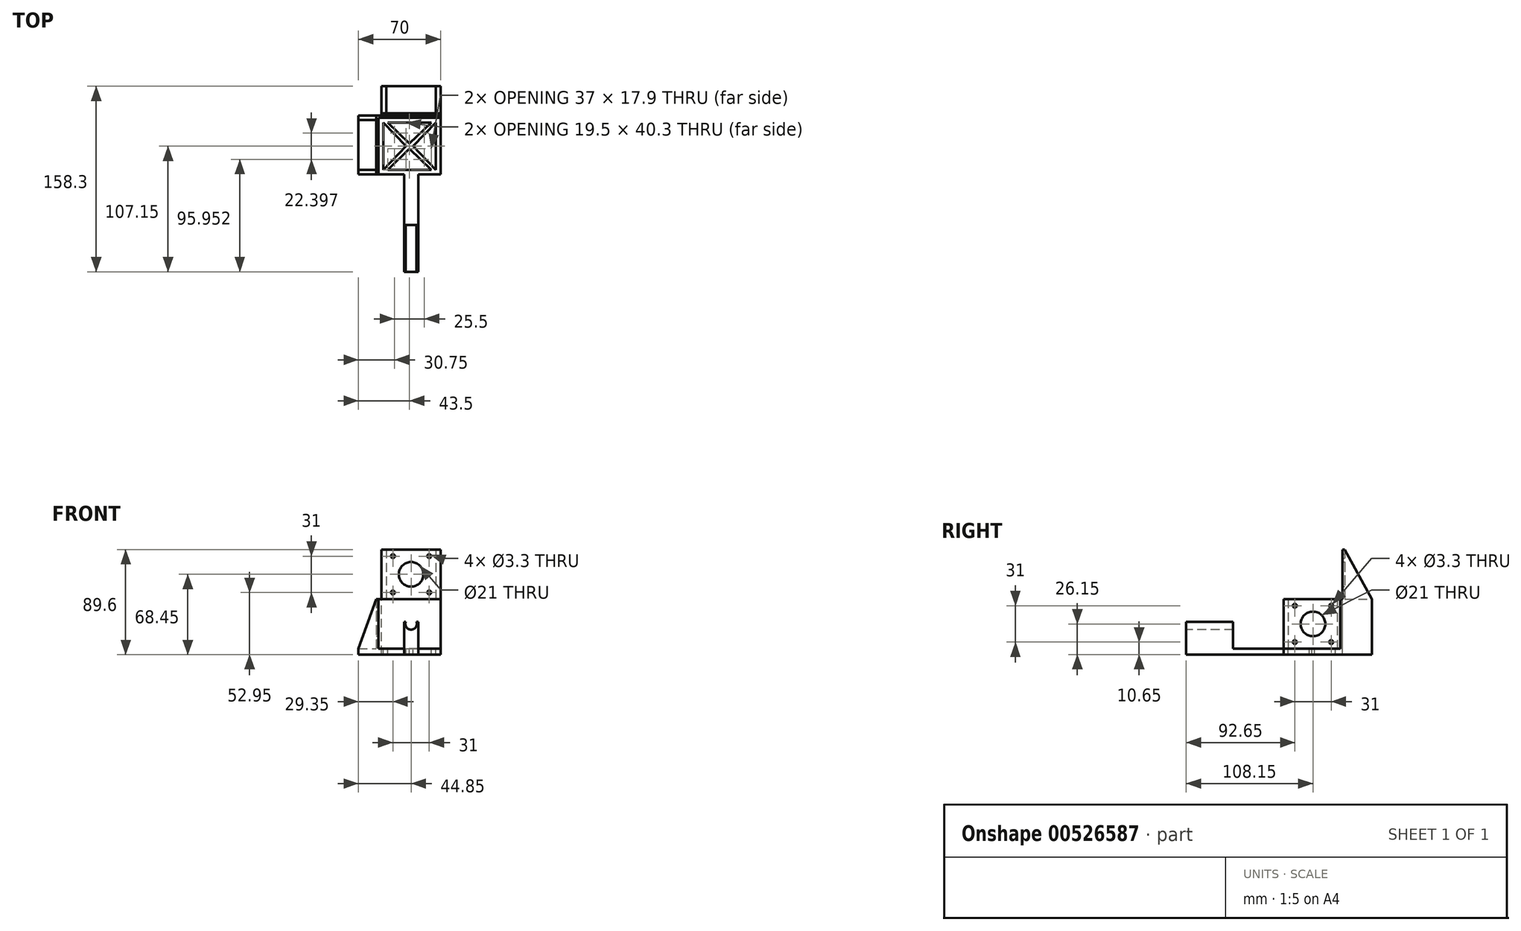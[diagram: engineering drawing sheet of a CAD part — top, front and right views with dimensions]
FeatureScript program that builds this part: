
annotation { "Feature Type Name" : "Feature", "Feature Type Description" : "" }
export const myFeature = defineFeature(function(context is Context, id is Id, definition is map)
    precondition{}
    {
        {
            var Q0;
            Q0=qCreatedBy(makeId("Top.planeOp"),FACE);
            var sketch = newSketch(context, id + "F0", { "sketchPlane" : qUnion([Q0])});
            skLineSegment(sketch, "E0.bottom", {"start": v(0, 0) * mm, "end": v(70, 0) * mm});
            skLineSegment(sketch, "E0.top", {"start": v(0, 80) * mm, "end": v(70, 80) * mm});
            skLineSegment(sketch, "E0.left", {"start": v(0, 0) * mm, "end": v(0, 80) * mm});
            skLineSegment(sketch, "E0.right", {"start": v(70, 0) * mm, "end": v(70, 80) * mm});
            skSolve(sketch);
        }
        {
            var Q0;
            Q0 = qSketchRegion(id + "F0", true);
            extrude(context, id + "F1", {"entities" : qUnion([Q0]), "depth" : 5 * mm, "offsetDistance" : 25 * mm});
        }
        {
            var Q0;
            Q0=makeQuery(id+"F1.opExtrude","CAP_FACE",FACE,{"disambiguationData":[OSD([sQuery(id+"F0.wireOp",EDGE,"E0.bottom"),sQuery(id+"F0.wireOp",EDGE,"E0.top"),sQuery(id+"F0.wireOp",EDGE,"E0.left"),sQuery(id+"F0.wireOp",EDGE,"E0.right")])],"isStart":false});
            var sketch = newSketch(context, id + "F2", { "sketchPlane" : qUnion([Q0])});
            skLineSegment(sketch, "E1.bottom", {"start": v(15, 46.3) * mm, "end": v(17, 46.3) * mm});
            skLineSegment(sketch, "E1.top", {"start": v(15, 4) * mm, "end": v(17, 4) * mm});
            skLineSegment(sketch, "E1.left", {"start": v(15, 46.3) * mm, "end": v(15, 4) * mm});
            skLineSegment(sketch, "E1.right", {"start": v(17, 46.3) * mm, "end": v(17, 4) * mm});
            skSolve(sketch);
        }
        {
            var Q0;
            Q0 = qSketchRegion(id + "F2", true);
            extrude(context, id + "F3", {"entities" : qUnion([Q0]), "operationType" : NewBodyOperationType.ADD, "depth" : 42.3 * mm, "offsetDistance" : 25 * mm});
        }
        {
            var Q0;
            Q0=makeQuery(id+"F3.opExtrude","SWEPT_FACE",FACE,{"disambiguationData":[OSD([sQuery(id+"F2.wireOp",EDGE,"E1.left")])]});
            var sketch = newSketch(context, id + "F4", { "sketchPlane" : qUnion([Q0])});
            skLineSegment(sketch, "E2.bottom", {"start": v(-9.65, 41.65) * mm, "end": v(-40.65, 41.65) * mm, "construction": true});
            skLineSegment(sketch, "E2.top", {"start": v(-9.65, 10.65) * mm, "end": v(-40.65, 10.65) * mm, "construction": true});
            skLineSegment(sketch, "E2.left", {"start": v(-9.65, 41.65) * mm, "end": v(-9.65, 10.65) * mm, "construction": true});
            skLineSegment(sketch, "E2.right", {"start": v(-40.65, 41.65) * mm, "end": v(-40.65, 10.65) * mm, "construction": true});
            skPoint(sketch, "E2.middle", {"position": v(-25.15, 26.15) * mm});
            skLineSegment(sketch, "E3", {"start": v(-25.15, 47.3) * mm, "end": v(-25.15, 5) * mm, "construction": true});
            skPoint(sketch, "E3.startSnap0", {"position": v(-25.15, 41.65) * mm});
            skPoint(sketch, "E3.endSnap0", {"position": v(-25.15, 5) * mm});
            skCircle(sketch, "E4", {"center": v(-40.65, 41.65) * mm, "radius": 1.65 * mm});
            skCircle(sketch, "E5", {"center": v(-9.65, 41.65) * mm, "radius": 1.65 * mm});
            skCircle(sketch, "E6", {"center": v(-9.65, 10.65) * mm, "radius": 1.65 * mm});
            skCircle(sketch, "E7", {"center": v(-40.65, 10.65) * mm, "radius": 1.65 * mm});
            skCircle(sketch, "E8", {"center": v(-25.15, 26.15) * mm, "radius": 10.5 * mm});
            skSolve(sketch);
        }
        {
            var Q0;
            Q0 = qSketchRegion(id + "F4", true);
            extrude(context, id + "F5", {"entities" : qUnion([Q0]), "operationType" : NewBodyOperationType.REMOVE, "oppositeDirection" : true, "depth" : 25 * mm, "offsetDistance" : 25 * mm});
        }
        {
            var Q0;
            Q0=makeQuery(id+"F3.opExtrude","SWEPT_FACE",FACE,{"disambiguationData":[OSD([sQuery(id+"F2.wireOp",EDGE,"E1.bottom")])]});
            var sketch = newSketch(context, id + "F6", { "sketchPlane" : qUnion([Q0])});
            skLineSegment(sketch, "E9", {"start": v(0, 5) * mm, "end": v(-17, 5) * mm});
            skLineSegment(sketch, "E10", {"start": v(-17, 47.3) * mm, "end": v(-17, 5) * mm});
            skLineSegment(sketch, "E11", {"start": v(0, 5) * mm, "end": v(-15, 47.3) * mm});
            skLineSegment(sketch, "E12", {"start": v(-15, 47.3) * mm, "end": v(-17, 47.3) * mm});
            skSolve(sketch);
        }
        {
            var Q0;
            Q0 = qSketchRegion(id + "F6", true);
            extrude(context, id + "F7", {"entities" : qUnion([Q0]), "operationType" : NewBodyOperationType.ADD, "depth" : 4 * mm, "offsetDistance" : 25 * mm});
        }
        {
            var Q0;
            Q0=makeQuery(id+"F3.opExtrude","SWEPT_FACE",FACE,{"disambiguationData":[OSD([sQuery(id+"F2.wireOp",EDGE,"E1.top")])]});
            var sketch = newSketch(context, id + "F8", { "sketchPlane" : qUnion([Q0])});
            skLineSegment(sketch, "E13", {"start": v(17, 47.3) * mm, "end": v(15, 47.3) * mm});
            skLineSegment(sketch, "E14", {"start": v(15, 47.3) * mm, "end": v(0, 5) * mm});
            skLineSegment(sketch, "E15", {"start": v(0, 5) * mm, "end": v(15, 5) * mm});
            skLineSegment(sketch, "E16", {"start": v(15, 5) * mm, "end": v(17, 5) * mm});
            skLineSegment(sketch, "E17", {"start": v(17, 5) * mm, "end": v(17, 47.3) * mm});
            skSolve(sketch);
        }
        {
            var Q0;
            Q0 = qSketchRegion(id + "F8", true);
            extrude(context, id + "F9", {"entities" : qUnion([Q0]), "operationType" : NewBodyOperationType.ADD, "depth" : 4 * mm, "offsetDistance" : 25 * mm});
        }
        {
            var Q0;
            {var subQ0=sQuery(id+"F0.wireOp",EDGE,"E0.left");var subQ2=sQuery(id+"F0.wireOp",EDGE,"E0.top");var subQ4=sQuery(id+"F0.wireOp",EDGE,"E0.right");var subQ5=sQuery(id+"F0.wireOp",EDGE,"E0.bottom");Q0=makeQuery(id+"F9.boolean.opBoolean","SPLIT",FACE,{"disambiguationData":[TD([makeQuery(id+"F1.opExtrude","SWEPT_FACE",FACE,{"disambiguationData":[OSD([subQ5])]})])],"derivedFrom":makeQuery(id+"F1.opExtrude","CAP_FACE",FACE,{"disambiguationData":[OSD([subQ5,subQ2,subQ0,subQ4])],"isStart":false})});}
            var sketch = newSketch(context, id + "F10", { "sketchPlane" : qUnion([Q0])});
            skLineSegment(sketch, "E18.bottom", {"start": v(0, 50.3) * mm, "end": v(70, 50.3) * mm});
            skLineSegment(sketch, "E18.left", {"start": v(0, 50.3) * mm, "end": v(0, 80) * mm});
            skLineSegment(sketch, "E18.right", {"start": v(70, 50.3) * mm, "end": v(70, 80) * mm});
            skLineSegment(sketch, "E19", {"start": v(0, 80) * mm, "end": v(70, 80) * mm});
            skSolve(sketch);
        }
        {
            var Q0;
            Q0 = qSketchRegion(id + "F10", true);
            extrude(context, id + "F11", {"entities" : qUnion([Q0]), "operationType" : NewBodyOperationType.ADD, "depth" : 42.3 * mm, "offsetDistance" : 25 * mm});
        }
        {
            var Q0;
            Q0=makeQuery(id+"F11.boolean.opBoolean","MERGE",FACE,{"derivedFrom":[makeQuery(id+"F9.boolean.opBoolean","MERGE",FACE,{"derivedFrom":[makeQuery(id+"F7.boolean.opBoolean","MERGE",FACE,{"derivedFrom":[makeQuery(id+"F3.opExtrude","CAP_FACE",FACE,{"disambiguationData":[OSD([sQuery(id+"F2.wireOp",EDGE,"E1.bottom"),sQuery(id+"F2.wireOp",EDGE,"E1.top"),sQuery(id+"F2.wireOp",EDGE,"E1.left"),sQuery(id+"F2.wireOp",EDGE,"E1.right")])],"isStart":false}),makeQuery(id+"F7.opExtrude","SWEPT_FACE",FACE,{"disambiguationData":[OSD([sQuery(id+"F6.wireOp",EDGE,"E12")])]})]}),makeQuery(id+"F9.opExtrude","SWEPT_FACE",FACE,{"disambiguationData":[OSD([sQuery(id+"F8.wireOp",EDGE,"E13")])]})]}),makeQuery(id+"F11.opExtrude","CAP_FACE",FACE,{"disambiguationData":[OSD([sQuery(id+"F10.wireOp",EDGE,"E18.bottom"),sQuery(id+"F10.wireOp",EDGE,"E18.top"),sQuery(id+"F10.wireOp",EDGE,"E18.left"),sQuery(id+"F10.wireOp",EDGE,"E18.right")])],"isStart":false})]});
            var sketch = newSketch(context, id + "F12", { "sketchPlane" : qUnion([Q0])});
            skLineSegment(sketch, "E20.bottom", {"start": v(66, 50.3) * mm, "end": v(23.7, 50.3) * mm});
            skLineSegment(sketch, "E20.top", {"start": v(66, 52.3) * mm, "end": v(23.7, 52.3) * mm});
            skLineSegment(sketch, "E20.left", {"start": v(66, 50.3) * mm, "end": v(66, 52.3) * mm});
            skLineSegment(sketch, "E20.right", {"start": v(23.7, 50.3) * mm, "end": v(23.7, 52.3) * mm});
            skSolve(sketch);
        }
        {
            var Q0;
            Q0 = qSketchRegion(id + "F12", true);
            extrude(context, id + "F13", {"entities" : qUnion([Q0]), "operationType" : NewBodyOperationType.ADD, "depth" : 42.3 * mm, "offsetDistance" : 25 * mm});
        }
        {
            var Q0;
            Q0=makeQuery(id+"F13.opExtrude","SWEPT_FACE",FACE,{"disambiguationData":[OSD([sQuery(id+"F12.wireOp",EDGE,"E20.top")])]});
            var sketch = newSketch(context, id + "F14", { "sketchPlane" : qUnion([Q0])});
            skLineSegment(sketch, "E21", {"start": v(-44.85, 89.6) * mm, "end": v(-44.85, 47.3) * mm, "construction": true});
            skLineSegment(sketch, "E22.bottom", {"start": v(-29.35, 83.95) * mm, "end": v(-60.35, 83.95) * mm, "construction": true});
            skLineSegment(sketch, "E22.top", {"start": v(-29.35, 52.95) * mm, "end": v(-60.35, 52.95) * mm, "construction": true});
            skLineSegment(sketch, "E22.left", {"start": v(-29.35, 83.95) * mm, "end": v(-29.35, 52.95) * mm, "construction": true});
            skLineSegment(sketch, "E22.right", {"start": v(-60.35, 83.95) * mm, "end": v(-60.35, 52.95) * mm, "construction": true});
            skPoint(sketch, "E22.middle", {"position": v(-44.85, 68.45) * mm});
            skCircle(sketch, "E23", {"center": v(-60.35, 83.95) * mm, "radius": 1.65 * mm});
            skCircle(sketch, "E24", {"center": v(-29.35, 83.95) * mm, "radius": 1.65 * mm});
            skCircle(sketch, "E25", {"center": v(-29.35, 52.95) * mm, "radius": 1.65 * mm});
            skCircle(sketch, "E26", {"center": v(-60.35, 52.95) * mm, "radius": 1.65 * mm});
            skCircle(sketch, "E27", {"center": v(-44.85, 68.45) * mm, "radius": 10.5 * mm});
            skSolve(sketch);
        }
        {
            var Q0;
            Q0 = qSketchRegion(id + "F14", true);
            extrude(context, id + "F15", {"entities" : qUnion([Q0]), "operationType" : NewBodyOperationType.REMOVE, "oppositeDirection" : true, "depth" : 25 * mm, "offsetDistance" : 25 * mm});
        }
        {
            var Q0;
            Q0=makeQuery(id+"F13.opExtrude","SWEPT_FACE",FACE,{"disambiguationData":[OSD([sQuery(id+"F12.wireOp",EDGE,"E20.left")])]});
            var sketch = newSketch(context, id + "F16", { "sketchPlane" : qUnion([Q0])});
            skLineSegment(sketch, "E28", {"start": v(50.3, 89.6) * mm, "end": v(52.3, 89.6) * mm});
            skLineSegment(sketch, "E29", {"start": v(52.3, 89.6) * mm, "end": v(75.3, 47.3) * mm});
            skLineSegment(sketch, "E30", {"start": v(75.3, 47.3) * mm, "end": v(50.3, 47.3) * mm});
            skLineSegment(sketch, "E31", {"start": v(50.3, 89.6) * mm, "end": v(50.3, 47.3) * mm});
            skSolve(sketch);
        }
        {
            var Q0;
            Q0 = qSketchRegion(id + "F16", true);
            extrude(context, id + "F17", {"entities" : qUnion([Q0]), "operationType" : NewBodyOperationType.ADD, "depth" : 4 * mm, "offsetDistance" : 25 * mm});
        }
        {
            var Q0;
            {var subQ1=sQuery(id+"F10.wireOp",EDGE,"E18.bottom");Q0=makeQuery(id+"F11.boolean.opBoolean","SPLIT",FACE,{"disambiguationData":[TD([makeQuery(id+"F1.opExtrude","SWEPT_FACE",FACE,{"disambiguationData":[OSD([sQuery(id+"F0.wireOp",EDGE,"E0.left")])]})])],"derivedFrom":makeQuery(id+"F11.opExtrude","SWEPT_FACE",FACE,{"disambiguationData":[OSD([subQ1])]})});}
            var sketch = newSketch(context, id + "F18", { "sketchPlane" : qUnion([Q0])});
            skLineSegment(sketch, "E32", {"start": v(15, 47.3) * mm, "end": v(0, 5) * mm});
            skLineSegment(sketch, "E33", {"start": v(0, 5) * mm, "end": v(0, 47.3) * mm});
            skLineSegment(sketch, "E34", {"start": v(0, 47.3) * mm, "end": v(15, 47.3) * mm});
            skSolve(sketch);
        }
        {
            var Q0;
            Q0 = qSketchRegion(id + "F18", true);
            extrude(context, id + "F19", {"entities" : qUnion([Q0]), "operationType" : NewBodyOperationType.REMOVE, "oppositeDirection" : true, "depth" : 88.9 * mm, "offsetDistance" : 25 * mm});
        }
        {
            var Q0;
            Q0=makeQuery(id+"F13.opExtrude","SWEPT_FACE",FACE,{"disambiguationData":[OSD([sQuery(id+"F12.wireOp",EDGE,"E20.right")])]});
            var sketch = newSketch(context, id + "F20", { "sketchPlane" : qUnion([Q0])});
            skLineSegment(sketch, "E35", {"start": v(-50.3, 89.6) * mm, "end": v(-52.3, 89.6) * mm});
            skLineSegment(sketch, "E36", {"start": v(-52.3, 89.6) * mm, "end": v(-75.3, 47.3) * mm});
            skLineSegment(sketch, "E37", {"start": v(-75.3, 47.3) * mm, "end": v(-50.3, 47.3) * mm});
            skLineSegment(sketch, "E38", {"start": v(-50.3, 47.3) * mm, "end": v(-50.3, 89.6) * mm});
            skSolve(sketch);
        }
        {
            var Q0;
            Q0 = qSketchRegion(id + "F20", true);
            extrude(context, id + "F21", {"entities" : qUnion([Q0]), "operationType" : NewBodyOperationType.ADD, "depth" : 4 * mm, "offsetDistance" : 25 * mm});
        }
        {
            var Q0;
            Q0=makeQuery(id+"F11.boolean.opBoolean","MERGE",FACE,{"derivedFrom":[makeQuery(id+"F9.boolean.opBoolean","MERGE",FACE,{"derivedFrom":[makeQuery(id+"F7.boolean.opBoolean","MERGE",FACE,{"derivedFrom":[makeQuery(id+"F3.opExtrude","CAP_FACE",FACE,{"disambiguationData":[OSD([sQuery(id+"F2.wireOp",EDGE,"E1.bottom"),sQuery(id+"F2.wireOp",EDGE,"E1.top"),sQuery(id+"F2.wireOp",EDGE,"E1.left"),sQuery(id+"F2.wireOp",EDGE,"E1.right")])],"isStart":false}),makeQuery(id+"F7.opExtrude","SWEPT_FACE",FACE,{"disambiguationData":[OSD([sQuery(id+"F6.wireOp",EDGE,"E12")])]})]}),makeQuery(id+"F9.opExtrude","SWEPT_FACE",FACE,{"disambiguationData":[OSD([sQuery(id+"F8.wireOp",EDGE,"E13")])]})]}),makeQuery(id+"F11.opExtrude","CAP_FACE",FACE,{"disambiguationData":[OSD([sQuery(id+"F10.wireOp",EDGE,"E18.bottom"),sQuery(id+"F10.wireOp",EDGE,"E18.left"),sQuery(id+"F10.wireOp",EDGE,"E18.right"),sQuery(id+"F10.wireOp",EDGE,"E19")])],"isStart":false})]});
            var sketch = newSketch(context, id + "F22", { "sketchPlane" : qUnion([Q0])});
            skLineSegment(sketch, "E39.bottom", {"start": v(19.7, 50.3) * mm, "end": v(0, 50.3) * mm});
            skLineSegment(sketch, "E39.top", {"start": v(19.7, 80) * mm, "end": v(0, 80) * mm});
            skLineSegment(sketch, "E39.left", {"start": v(19.7, 50.3) * mm, "end": v(19.7, 80) * mm});
            skLineSegment(sketch, "E39.right", {"start": v(0, 50.3) * mm, "end": v(0, 80) * mm});
            skSolve(sketch);
        }
        {
            var Q0;
            Q0 = qSketchRegion(id + "F22", true);
            extrude(context, id + "F23", {"entities" : qUnion([Q0]), "operationType" : NewBodyOperationType.REMOVE, "oppositeDirection" : true, "depth" : 64.9 * mm, "offsetDistance" : 25 * mm});
        }
        {
            var Q0;
            {var subQ4=sQuery(id+"F8.wireOp",EDGE,"E13");var subQ7=sQuery(id+"F2.wireOp",EDGE,"E1.left");var subQ8=sQuery(id+"F6.wireOp",EDGE,"E12");var subQ9=sQuery(id+"F2.wireOp",EDGE,"E1.right");Q0=makeQuery(id+"F23.boolean.opBoolean","SPLIT",FACE,{"disambiguationData":[TD([makeQuery(id+"F1.opExtrude","SWEPT_FACE",FACE,{"disambiguationData":[OSD([sQuery(id+"F0.wireOp",EDGE,"E0.bottom")])]})])],"derivedFrom":makeQuery(id+"F11.boolean.opBoolean","MERGE",FACE,{"derivedFrom":[makeQuery(id+"F9.boolean.opBoolean","MERGE",FACE,{"derivedFrom":[makeQuery(id+"F7.boolean.opBoolean","MERGE",FACE,{"derivedFrom":[makeQuery(id+"F3.opExtrude","CAP_FACE",FACE,{"disambiguationData":[OSD([sQuery(id+"F2.wireOp",EDGE,"E1.bottom"),sQuery(id+"F2.wireOp",EDGE,"E1.top"),subQ7,subQ9])],"isStart":false}),makeQuery(id+"F7.opExtrude","SWEPT_FACE",FACE,{"disambiguationData":[OSD([subQ8])]})]}),makeQuery(id+"F9.opExtrude","SWEPT_FACE",FACE,{"disambiguationData":[OSD([subQ4])]})]}),makeQuery(id+"F11.opExtrude","CAP_FACE",FACE,{"disambiguationData":[OSD([sQuery(id+"F10.wireOp",EDGE,"E18.bottom"),sQuery(id+"F10.wireOp",EDGE,"E18.left"),sQuery(id+"F10.wireOp",EDGE,"E18.right"),sQuery(id+"F10.wireOp",EDGE,"E19")])],"isStart":false})]})});}
            var sketch = newSketch(context, id + "F24", { "sketchPlane" : qUnion([Q0])});
            skLineSegment(sketch, "E40.bottom", {"start": v(17, 50.3) * mm, "end": v(70, 50.3) * mm});
            skLineSegment(sketch, "E40.top", {"start": v(17, 48.3) * mm, "end": v(70, 48.3) * mm});
            skLineSegment(sketch, "E40.left", {"start": v(17, 50.3) * mm, "end": v(17, 48.3) * mm});
            skLineSegment(sketch, "E40.right", {"start": v(70, 50.3) * mm, "end": v(70, 48.3) * mm});
            skSolve(sketch);
        }
        {
            var Q0;
            Q0 = qSketchRegion(id + "F24", true);
            extrude(context, id + "F25", {"entities" : qUnion([Q0]), "operationType" : NewBodyOperationType.ADD, "oppositeDirection" : true, "depth" : 45.92 * mm, "offsetDistance" : 25 * mm});
        }
        {
            var Q0;
            {var subQ5=sQuery(id+"F10.wireOp",EDGE,"E18.right");var subQ9=sQuery(id+"F10.wireOp",EDGE,"E19");Q0=makeQuery(id+"F23.boolean.opBoolean","SPLIT",FACE,{"disambiguationData":[TD([makeQuery(id+"F1.opExtrude","SWEPT_FACE",FACE,{"disambiguationData":[OSD([sQuery(id+"F0.wireOp",EDGE,"E0.top")])]})])],"derivedFrom":makeQuery(id+"F11.boolean.opBoolean","MERGE",FACE,{"derivedFrom":[makeQuery(id+"F9.boolean.opBoolean","MERGE",FACE,{"derivedFrom":[makeQuery(id+"F7.boolean.opBoolean","MERGE",FACE,{"derivedFrom":[makeQuery(id+"F3.opExtrude","CAP_FACE",FACE,{"disambiguationData":[OSD([sQuery(id+"F2.wireOp",EDGE,"E1.bottom"),sQuery(id+"F2.wireOp",EDGE,"E1.top"),sQuery(id+"F2.wireOp",EDGE,"E1.left"),sQuery(id+"F2.wireOp",EDGE,"E1.right")])],"isStart":false}),makeQuery(id+"F7.opExtrude","SWEPT_FACE",FACE,{"disambiguationData":[OSD([sQuery(id+"F6.wireOp",EDGE,"E12")])]})]}),makeQuery(id+"F9.opExtrude","SWEPT_FACE",FACE,{"disambiguationData":[OSD([sQuery(id+"F8.wireOp",EDGE,"E13")])]})]}),makeQuery(id+"F11.opExtrude","CAP_FACE",FACE,{"disambiguationData":[OSD([sQuery(id+"F10.wireOp",EDGE,"E18.bottom"),sQuery(id+"F10.wireOp",EDGE,"E18.left"),subQ5,subQ9])],"isStart":false})]})});}
            var sketch = newSketch(context, id + "F26", { "sketchPlane" : qUnion([Q0])});
            skLineSegment(sketch, "E41.bottom", {"start": v(70, 75.3) * mm, "end": v(19.7, 75.3) * mm});
            skLineSegment(sketch, "E41.top", {"start": v(70, 80) * mm, "end": v(19.7, 80) * mm});
            skLineSegment(sketch, "E41.left", {"start": v(70, 75.3) * mm, "end": v(70, 80) * mm});
            skLineSegment(sketch, "E41.right", {"start": v(19.7, 75.3) * mm, "end": v(19.7, 80) * mm});
            skSolve(sketch);
        }
        {
            var Q0;
            Q0 = qSketchRegion(id + "F26", true);
            extrude(context, id + "F27", {"entities" : qUnion([Q0]), "operationType" : NewBodyOperationType.REMOVE, "oppositeDirection" : true, "depth" : 73.2 * mm, "offsetDistance" : 25 * mm});
        }
        {
            var Q0;
            {var subQ0=sQuery(id+"F0.wireOp",EDGE,"E0.left");var subQ2=sQuery(id+"F0.wireOp",EDGE,"E0.top");var subQ4=sQuery(id+"F0.wireOp",EDGE,"E0.right");var subQ5=sQuery(id+"F0.wireOp",EDGE,"E0.bottom");Q0=makeQuery(id+"F9.boolean.opBoolean","SPLIT",FACE,{"disambiguationData":[TD([makeQuery(id+"F1.opExtrude","SWEPT_FACE",FACE,{"disambiguationData":[OSD([subQ5])]})])],"derivedFrom":makeQuery(id+"F1.opExtrude","CAP_FACE",FACE,{"disambiguationData":[OSD([subQ5,subQ2,subQ0,subQ4])],"isStart":false})});}
            var sketch = newSketch(context, id + "F28", { "sketchPlane" : qUnion([Q0])});
            skLineSegment(sketch, "E42.bottom", {"start": v(38.85, 0) * mm, "end": v(50.85, 0) * mm});
            skLineSegment(sketch, "E42.top", {"start": v(38.85, -83) * mm, "end": v(50.85, -83) * mm});
            skLineSegment(sketch, "E42.left", {"start": v(38.85, 0) * mm, "end": v(38.85, -83) * mm});
            skLineSegment(sketch, "E42.right", {"start": v(50.85, 0) * mm, "end": v(50.85, -83) * mm});
            skLineSegment(sketch, "E43", {"start": v(44.85, 0) * mm, "end": v(44.85, 48.3) * mm, "construction": true});
            skSolve(sketch);
        }
        {
            var Q0;
            Q0 = qSketchRegion(id + "F28", true);
            extrude(context, id + "F29", {"entities" : qUnion([Q0]), "operationType" : NewBodyOperationType.ADD, "oppositeDirection" : true, "depth" : 5 * mm, "offsetDistance" : 25 * mm});
        }
        {
            var Q0;
            {var subQ0=sQuery(id+"F0.wireOp",EDGE,"E0.left");var subQ2=sQuery(id+"F0.wireOp",EDGE,"E0.top");var subQ4=sQuery(id+"F0.wireOp",EDGE,"E0.right");var subQ5=sQuery(id+"F0.wireOp",EDGE,"E0.bottom");Q0=makeQuery(id+"F29.boolean.opBoolean","MERGE",FACE,{"derivedFrom":[makeQuery(id+"F9.boolean.opBoolean","SPLIT",FACE,{"disambiguationData":[TD([makeQuery(id+"F1.opExtrude","SWEPT_FACE",FACE,{"disambiguationData":[OSD([subQ5])]})])],"derivedFrom":makeQuery(id+"F1.opExtrude","CAP_FACE",FACE,{"disambiguationData":[OSD([subQ5,subQ2,subQ0,subQ4])],"isStart":false})}),makeQuery(id+"F29.opExtrude","CAP_FACE",FACE,{"disambiguationData":[OSD([sQuery(id+"F28.wireOp",EDGE,"E42.bottom"),sQuery(id+"F28.wireOp",EDGE,"E42.top"),sQuery(id+"F28.wireOp",EDGE,"E42.left"),sQuery(id+"F28.wireOp",EDGE,"E42.right")])],"isStart":true})]});}
            var sketch = newSketch(context, id + "F30", { "sketchPlane" : qUnion([Q0])});
            skLineSegment(sketch, "E44.bottom", {"start": v(38.85, -83) * mm, "end": v(50.85, -83) * mm});
            skLineSegment(sketch, "E44.top", {"start": v(38.85, -43) * mm, "end": v(50.85, -43) * mm});
            skLineSegment(sketch, "E44.left", {"start": v(38.85, -83) * mm, "end": v(38.85, -43) * mm});
            skLineSegment(sketch, "E44.right", {"start": v(50.85, -83) * mm, "end": v(50.85, -43) * mm});
            skSolve(sketch);
        }
        {
            var Q0;
            Q0 = qSketchRegion(id + "F30", true);
            extrude(context, id + "F31", {"entities" : qUnion([Q0]), "operationType" : NewBodyOperationType.ADD, "depth" : 23 * mm, "offsetDistance" : 25 * mm});
        }
        {
            var Q0;
            Q0=makeQuery(id+"F31.boolean.opBoolean","MERGE",FACE,{"derivedFrom":[makeQuery(id+"F29.opExtrude","SWEPT_FACE",FACE,{"disambiguationData":[OSD([sQuery(id+"F28.wireOp",EDGE,"E42.top")])]}),makeQuery(id+"F31.opExtrude","SWEPT_FACE",FACE,{"disambiguationData":[OSD([sQuery(id+"F30.wireOp",EDGE,"E44.bottom")])]})]});
            var sketch = newSketch(context, id + "F32", { "sketchPlane" : qUnion([Q0])});
            skCircle(sketch, "E45", {"center": v(44.85, 26.15) * mm, "radius": 4.85 * mm});
            skPoint(sketch, "E45.centerSnap0", {"position": v(44.85, 28) * mm});
            skSolve(sketch);
        }
        {
            var Q0;
            Q0 = qSketchRegion(id + "F32", true);
            extrude(context, id + "F33", {"entities" : qUnion([Q0]), "operationType" : NewBodyOperationType.REMOVE, "oppositeDirection" : true, "depth" : 45.2 * mm, "offsetDistance" : 25 * mm});
        }
        {
            var Q0;
            {var subQ0=sQuery(id+"F0.wireOp",EDGE,"E0.left");var subQ2=sQuery(id+"F0.wireOp",EDGE,"E0.top");var subQ4=sQuery(id+"F0.wireOp",EDGE,"E0.right");var subQ5=sQuery(id+"F0.wireOp",EDGE,"E0.bottom");Q0=makeQuery(id+"F29.boolean.opBoolean","MERGE",FACE,{"derivedFrom":[makeQuery(id+"F9.boolean.opBoolean","SPLIT",FACE,{"disambiguationData":[TD([makeQuery(id+"F1.opExtrude","SWEPT_FACE",FACE,{"disambiguationData":[OSD([subQ5])]})])],"derivedFrom":makeQuery(id+"F1.opExtrude","CAP_FACE",FACE,{"disambiguationData":[OSD([subQ5,subQ2,subQ0,subQ4])],"isStart":false})}),makeQuery(id+"F29.opExtrude","CAP_FACE",FACE,{"disambiguationData":[OSD([sQuery(id+"F28.wireOp",EDGE,"E42.bottom"),sQuery(id+"F28.wireOp",EDGE,"E42.top"),sQuery(id+"F28.wireOp",EDGE,"E42.left"),sQuery(id+"F28.wireOp",EDGE,"E42.right")])],"isStart":true})]});}
            var sketch = newSketch(context, id + "F34", { "sketchPlane" : qUnion([Q0])});
            skLineSegment(sketch, "E46", {"start": v(21, 44.3) * mm, "end": v(40.5, 24.15) * mm});
            skLineSegment(sketch, "E47", {"start": v(40.5, 24.15) * mm, "end": v(21, 4) * mm});
            skLineSegment(sketch, "E48", {"start": v(21, 4) * mm, "end": v(21, 44.3) * mm});
            skLineSegment(sketch, "E49", {"start": v(43.5, 48.3) * mm, "end": v(43.5, 0) * mm, "construction": true});
            skLineSegment(sketch, "E50.MirrorCS", {"start": v(66, 44.3) * mm, "end": v(46.5, 24.15) * mm});
            skLineSegment(sketch, "E51.MirrorCS", {"start": v(66, 4) * mm, "end": v(66, 44.3) * mm});
            skLineSegment(sketch, "E52.MirrorCS", {"start": v(46.5, 24.15) * mm, "end": v(66, 4) * mm});
            skLineSegment(sketch, "E53", {"start": v(25, 44.3) * mm, "end": v(43.5, 26.4) * mm});
            skLineSegment(sketch, "E54", {"start": v(43.5, 26.4) * mm, "end": v(62, 44.3) * mm});
            skLineSegment(sketch, "E55", {"start": v(62, 44.3) * mm, "end": v(25, 44.3) * mm});
            skLineSegment(sketch, "E56", {"start": v(40.5, 24.15) * mm, "end": v(46.5, 24.15) * mm, "construction": true});
            skLineSegment(sketch, "E57.MirrorCS", {"start": v(43.5, 21.9) * mm, "end": v(62, 4) * mm});
            skLineSegment(sketch, "E58.MirrorCS", {"start": v(62, 4) * mm, "end": v(25, 4) * mm});
            skLineSegment(sketch, "E59.MirrorCS", {"start": v(25, 4) * mm, "end": v(43.5, 21.9) * mm});
            skSolve(sketch);
        }
        {
            var Q0;
            Q0 = qSketchRegion(id + "F34", true);
            extrude(context, id + "F35", {"entities" : qUnion([Q0]), "operationType" : NewBodyOperationType.REMOVE, "oppositeDirection" : true, "depth" : 25 * mm, "offsetDistance" : 25 * mm});
        }
    });
